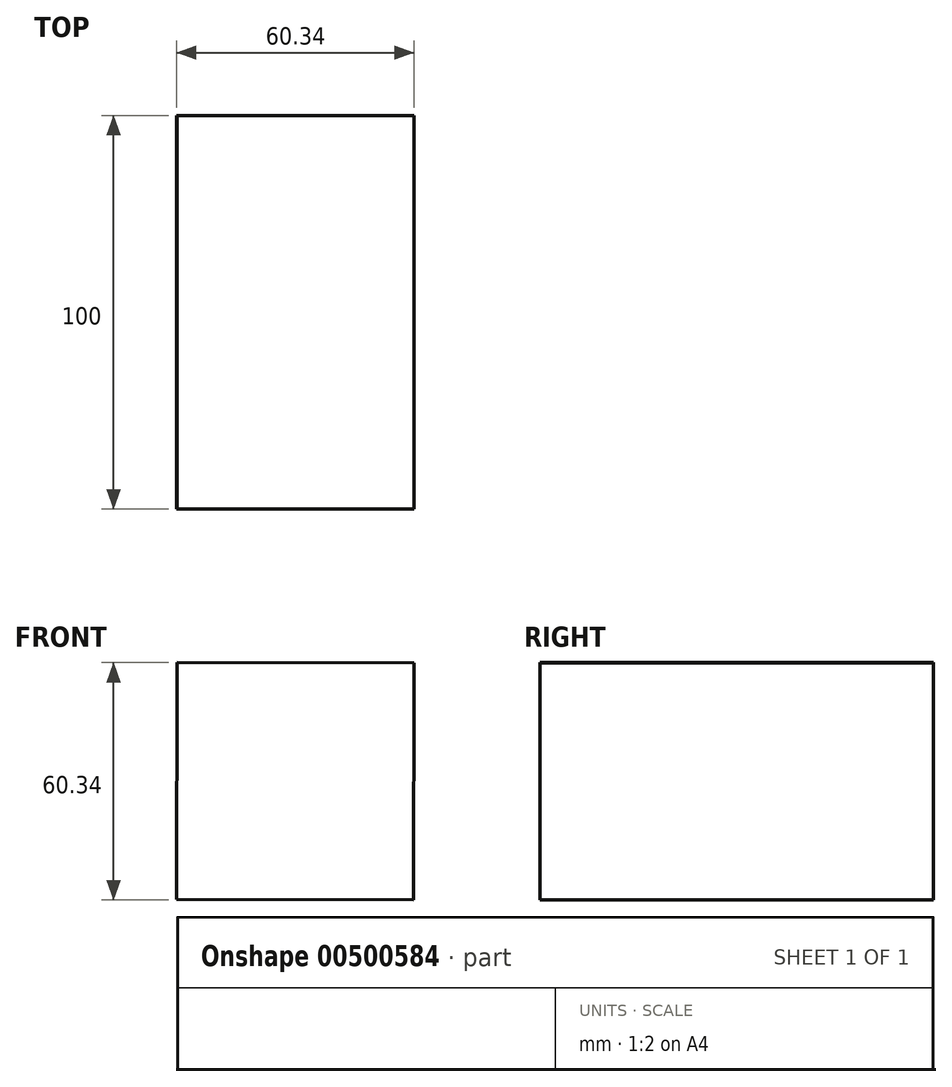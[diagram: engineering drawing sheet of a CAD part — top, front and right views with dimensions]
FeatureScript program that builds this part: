
annotation { "Feature Type Name" : "Feature", "Feature Type Description" : "" }
export const myFeature = defineFeature(function(context is Context, id is Id, definition is map)
    precondition{}
    {
        {
            var Q0;
            Q0=qCreatedBy(makeId("Front.planeOp"),FACE);
            var sketch = newSketch(context, id + "F0", { "sketchPlane" : qUnion([Q0])});
            skCircle(sketch, "E0.cCircle", {"center": v(0, 0) * mm, "radius": 42.56 * mm, "construction": true});
            skLineSegment(sketch, "E0.0", {"start": v(-30.02, 30.17) * mm, "end": v(30.17, 30.02) * mm});
            skLineSegment(sketch, "E0.1", {"start": v(30.17, 30.02) * mm, "end": v(30.02, -30.17) * mm});
            skLineSegment(sketch, "E0.2", {"start": v(30.02, -30.17) * mm, "end": v(-30.17, -30.02) * mm});
            skLineSegment(sketch, "E0.3", {"start": v(-30.17, -30.02) * mm, "end": v(-30.02, 30.17) * mm});
            skSolve(sketch);
        }
        {
            var Q0;
            Q0=makeQuery(id+"F0.imprint","IMPRINT",FACE,{"disambiguationData":[TD([[makeQuery(id+"F0.imprint","IMPRINT",EDGE,{"derivedFrom":sQuery(id+"F0.wireOp",EDGE,"E0.0")}),-1.0]])]});
            extrude(context, id + "F1", {"entities" : qUnion([Q0]), "endBound" : BoundingType.SYMMETRIC, "depth" : 100 * mm});
        }
    });
